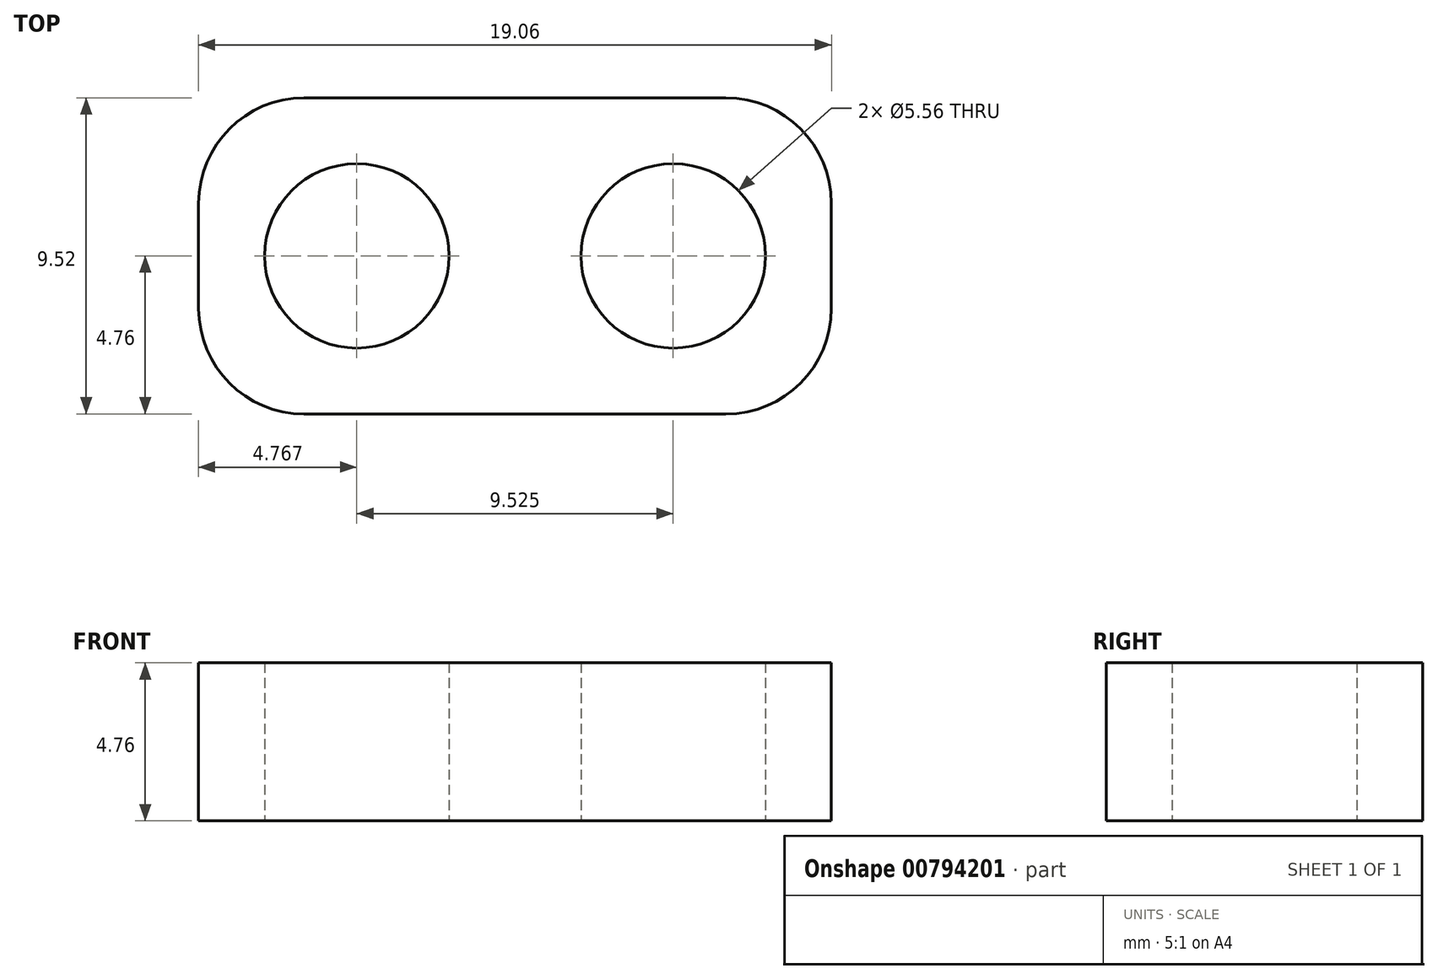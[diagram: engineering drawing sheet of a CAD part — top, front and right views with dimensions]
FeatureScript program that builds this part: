
annotation { "Feature Type Name" : "Feature", "Feature Type Description" : "" }
export const myFeature = defineFeature(function(context is Context, id is Id, definition is map)
    precondition{}
    {
        {
            var Q0;
            Q0=qCreatedBy(makeId("Top.planeOp"),FACE);
            var sketch = newSketch(context, id + "F0", { "sketchPlane" : qUnion([Q0])});
            skLineSegment(sketch, "E0.bottom", {"start": v(9.53, 4.76) * mm, "end": v(-9.53, 4.76) * mm});
            skLineSegment(sketch, "E0.top", {"start": v(9.53, -4.76) * mm, "end": v(-9.53, -4.76) * mm});
            skLineSegment(sketch, "E0.left", {"start": v(9.53, 4.76) * mm, "end": v(9.53, -4.76) * mm});
            skLineSegment(sketch, "E0.right", {"start": v(-9.53, 4.76) * mm, "end": v(-9.53, -4.76) * mm});
            skPoint(sketch, "E0.middle", {"position": v(0, 0) * mm});
            skCircle(sketch, "E1", {"center": v(-4.76, 0) * mm, "radius": 2.78 * mm});
            skCircle(sketch, "E2", {"center": v(4.76, 0) * mm, "radius": 2.78 * mm});
            skSolve(sketch);
        }
        {
            var Q0;
            Q0=makeQuery(id+"F0.imprint","IMPRINT",FACE,{"disambiguationData":[TD([[makeQuery(id+"F0.imprint","IMPRINT",EDGE,{"derivedFrom":sQuery(id+"F0.wireOp",EDGE,"E0.bottom")}),1.0]])]});
            extrude(context, id + "F1", {"entities" : qUnion([Q0]), "depth" : 4.76 * mm, "offsetDistance" : 25.4 * mm});
        }
        {
            var Q0;
            Q0=makeQuery(id+"F1.opExtrude","SWEPT_EDGE",EDGE,{"disambiguationData":[OSD([sQuery(id+"F0.wireOp",EDGE,"E0.top"),sQuery(id+"F0.wireOp",EDGE,"E0.right")])]});
            var Q1;
            Q1=makeQuery(id+"F1.opExtrude","SWEPT_EDGE",EDGE,{"disambiguationData":[OSD([sQuery(id+"F0.wireOp",EDGE,"E0.bottom"),sQuery(id+"F0.wireOp",EDGE,"E0.right")])]});
            var Q2;
            Q2=makeQuery(id+"F1.opExtrude","SWEPT_EDGE",EDGE,{"disambiguationData":[OSD([sQuery(id+"F0.wireOp",EDGE,"E0.top"),sQuery(id+"F0.wireOp",EDGE,"E0.left")])]});
            var Q3;
            Q3=makeQuery(id+"F1.opExtrude","SWEPT_EDGE",EDGE,{"disambiguationData":[OSD([sQuery(id+"F0.wireOp",EDGE,"E0.bottom"),sQuery(id+"F0.wireOp",EDGE,"E0.left")])]});
            fillet(context, id + "F2", {"entities" : qUnion([Q0, Q1, Q2, Q3]), "radius" : 3.17 * mm, "tangentPropagation" : true, "allowEdgeOverflow" : false});
        }
    });
